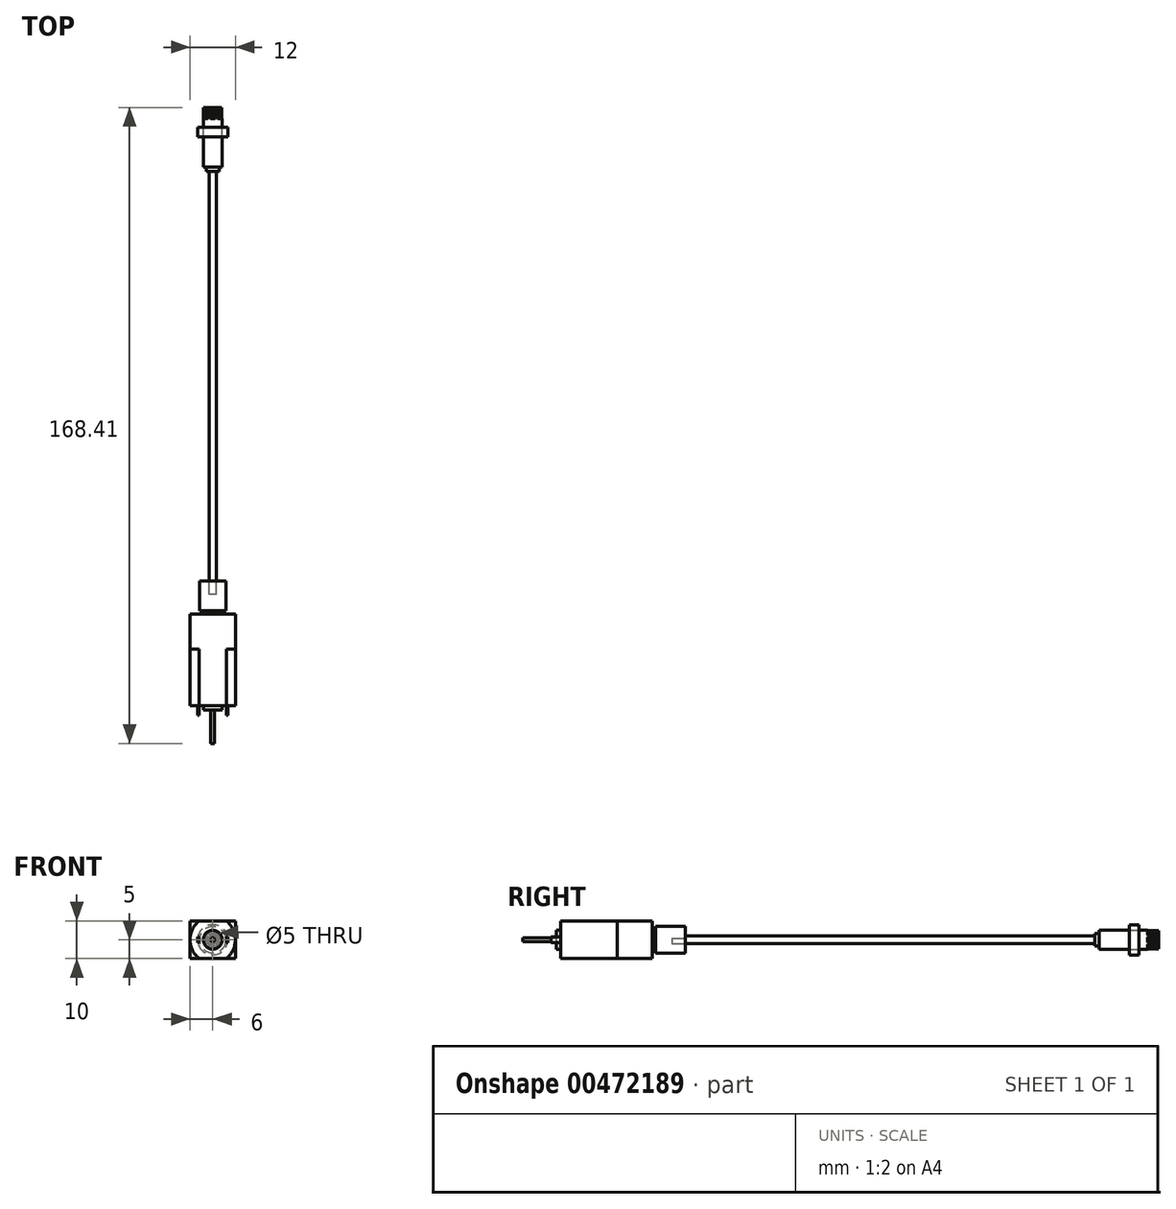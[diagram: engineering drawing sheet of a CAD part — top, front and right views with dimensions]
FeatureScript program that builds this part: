
annotation { "Feature Type Name" : "Feature", "Feature Type Description" : "" }
export const myFeature = defineFeature(function(context is Context, id is Id, definition is map)
    precondition{}
    {
        {
            var Q0;
            Q0=qCreatedBy(makeId("Right.planeOp"),FACE);
            var sketch = newSketch(context, id + "F0", { "sketchPlane" : qUnion([Q0])});
            skLineSegment(sketch, "E0.bottom", {"start": v(8.48, 0) * mm, "end": v(-8.48, 0) * mm});
            skLineSegment(sketch, "E0.top", {"start": v(8.48, 2.5) * mm, "end": v(-7.38, 2.5) * mm});
            skLineSegment(sketch, "E0.left", {"start": v(8.47, 0) * mm, "end": v(8.47, 2.5) * mm});
            skLineSegment(sketch, "E0.right", {"start": v(-8.48, 0) * mm, "end": v(-8.48, 1.7) * mm});
            skLineSegment(sketch, "E1", {"start": v(-8.48, 1.7) * mm, "end": v(-7.38, 1.7) * mm});
            skLineSegment(sketch, "E2", {"start": v(-7.38, 1.7) * mm, "end": v(-7.38, 2.5) * mm});
            skSolve(sketch);
        }
        {
            var Q0;
            Q0 = qSketchRegion(id + "F0", true);
            var Q1;
            Q1=sQuery(id+"F0.wireOp",EDGE,"E0.bottom");
            revolve(context, id + "F1", {"entities" : qUnion([Q0]), "axis" : qUnion([Q1]), "revolveType" : RevolveType.FULL});
        }
        {
            var Q0;
            Q0=makeQuery(id+"F1.opRevolve","SWEPT_FACE",FACE,{"disambiguationData":[OSD([sQuery(id+"F0.wireOp",EDGE,"E0.left")])]});
            var sketch = newSketch(context, id + "F2", { "sketchPlane" : qUnion([Q0])});
            skLineSegment(sketch, "E3", {"start": v(-0.25, 1.17) * mm, "end": v(0.25, 1.17) * mm});
            skPoint(sketch, "E4", {"position": v(0, 1.17) * mm});
            skLineSegment(sketch, "E5", {"start": v(-0.25, 1.17) * mm, "end": v(-0.6, 2.43) * mm});
            skLineSegment(sketch, "E6.MirrorCS", {"start": v(0.25, 1.17) * mm, "end": v(0.6, 2.43) * mm});
            skArc(sketch, "E7.0", {"start": v(0.6, 2.43) * mm, "mid": v(0, 2.5) * mm, "end": v(-0.6, 2.43) * mm});
            skPoint(sketch, "E8", {"position": v(0, 2.5) * mm});
            skSolve(sketch);
        }
        {
            var Q0;
            Q0 = qSketchRegion(id + "F2", true);
            extrude(context, id + "F3", {"entities" : qUnion([Q0]), "oppositeDirection" : true, "depth" : 3 * mm});
        }
        {
            var Q0;
            Q0=makeQuery(id+"F3.opExtrude","SWEPT_BODY",BODY,{"disambiguationData":[OSD([sQuery(id+"F2.wireOp",EDGE,"E3"),sQuery(id+"F2.wireOp",EDGE,"E5"),sQuery(id+"F2.wireOp",EDGE,"E6.MirrorCS"),sQuery(id+"F2.wireOp",EDGE,"E7.0")])]});
            var Q1;
            Q1=makeQuery(id+"F1.opRevolve","SWEPT_EDGE",EDGE,{"disambiguationData":[OSD([sQuery(id+"F0.wireOp",EDGE,"E0.top"),sQuery(id+"F0.wireOp",EDGE,"E0.left")])]});
            circularPattern(context, id + "F4", {"operationType" : NewBodyOperationType.REMOVE, "entities" : qUnion([Q0]), "axis" : qUnion([Q1]), "angle" : 360 * degree, "instanceCount" : 8, "equalSpace" : true});
        }
        {
            var Q0;
            Q0=qCreatedBy(makeId("Right.planeOp"),FACE);
            var sketch = newSketch(context, id + "F5", { "sketchPlane" : qUnion([Q0])});
            skLineSegment(sketch, "E9", {"start": v(3.18, 2.5) * mm, "end": v(3.18, 4) * mm});
            skLineSegment(sketch, "E10", {"start": v(3.18, 4) * mm, "end": v(0.68, 4) * mm});
            skLineSegment(sketch, "E11", {"start": v(0.68, 4) * mm, "end": v(0.68, 2.5) * mm});
            skLineSegment(sketch, "E12", {"start": v(0.68, 2.5) * mm, "end": v(3.18, 2.5) * mm});
            skSolve(sketch);
        }
        {
            var Q0;
            Q0 = qSketchRegion(id + "F5", true);
            var Q1;
            Q1=sQuery(id+"F0.wireOp",EDGE,"E0.bottom");
            revolve(context, id + "F6", {"entities" : qUnion([Q0]), "axis" : qUnion([Q1]), "revolveType" : RevolveType.FULL});
        }
        {
            var Q0;
            Q0=makeQuery(id+"F1.opRevolve","SWEPT_FACE",FACE,{"disambiguationData":[OSD([sQuery(id+"F0.wireOp",EDGE,"E0.right")])]});
            var sketch = newSketch(context, id + "F7", { "sketchPlane" : qUnion([Q0])});
            skCircle(sketch, "E13", {"center": v(0, 0) * mm, "radius": 1 * mm});
            skSolve(sketch);
        }
        {
            var Q0;
            Q0 = qSketchRegion(id + "F7", true);
            extrude(context, id + "F8", {"entities" : qUnion([Q0]), "depth" : 112.4 * mm});
        }
        {
            var Q0;
            Q0=makeQuery(id+"F8.opExtrude","CAP_FACE",FACE,{"disambiguationData":[OSD([sQuery(id+"F7.wireOp",EDGE,"E13")])],"isStart":false});
            var sketch = newSketch(context, id + "F9", { "sketchPlane" : qUnion([Q0])});
            skCircle(sketch, "E14", {"center": v(0, 0) * mm, "radius": 3.5 * mm});
            skSolve(sketch);
        }
        {
            var Q0;
            Q0 = qSketchRegion(id + "F9", true);
            extrude(context, id + "F10", {"entities" : qUnion([Q0]), "depth" : 7.8 * mm, "symmetric" : true});
        }
        {
            var Q0;
            Q0=makeQuery(id+"F10.opExtrude","CAP_FACE",FACE,{"disambiguationData":[OSD([sQuery(id+"F9.wireOp",EDGE,"E14")])],"isStart":true});
            var sketch = newSketch(context, id + "F11", { "sketchPlane" : qUnion([Q0])});
            skArc(sketch, "E15.0", {"start": v(-0.94, 0.34) * mm, "mid": v(0, -1) * mm, "end": v(0.94, 0.34) * mm});
            skLineSegment(sketch, "E16", {"start": v(-0.94, 0.34) * mm, "end": v(0.94, 0.34) * mm});
            skSolve(sketch);
        }
        {
            var Q0;
            Q0 = qSketchRegion(id + "F11", true);
            extrude(context, id + "F12", {"entities" : qUnion([Q0]), "operationType" : NewBodyOperationType.REMOVE, "oppositeDirection" : true, "depth" : 3.5 * mm});
        }
        {
            var Q0;
            Q0=makeQuery(id+"F10.opExtrude","SWEPT_BODY",BODY,{"disambiguationData":[OSD([sQuery(id+"F9.wireOp",EDGE,"E14")])]});
            var Q1;
            Q1=makeQuery(id+"F15.opExtrude","SWEPT_BODY",BODY,{"disambiguationData":[OSD([sQuery(id+"F14.wireOp",EDGE,"E17"),sQuery(id+"F14.wireOp",EDGE,"E18")])]});
            var Q2;
            Q2=makeQuery(id+"F8.opExtrude","SWEPT_BODY",BODY,{"disambiguationData":[OSD([sQuery(id+"F7.wireOp",EDGE,"E13")])]});
            booleanBodies(context, id + "F13", {"operationType" : BooleanOperationType.SUBTRACTION, "tools" : qUnion([Q0, Q1]), "targets" : qUnion([Q2]), "keepTools" : true});
        }
        {
            var Q0;
            Q0=makeQuery(id+"F10.opExtrude","CAP_FACE",FACE,{"disambiguationData":[OSD([sQuery(id+"F9.wireOp",EDGE,"E14")])],"isStart":false});
            var sketch = newSketch(context, id + "F14", { "sketchPlane" : qUnion([Q0])});
            skArc(sketch, "E17", {"start": v(-1.12, 1) * mm, "mid": v(0, -1.5) * mm, "end": v(1.12, 1) * mm});
            skLineSegment(sketch, "E18", {"start": v(-1.12, 1) * mm, "end": v(1.12, 1) * mm});
            skSolve(sketch);
        }
        {
            var Q0;
            Q0 = qSketchRegion(id + "F14", true);
            extrude(context, id + "F15", {"entities" : qUnion([Q0]), "oppositeDirection" : true, "depth" : 3.6 * mm});
        }
        {
            var Q0;
            Q0=makeQuery(id+"F15.opExtrude","SWEPT_BODY",BODY,{"disambiguationData":[OSD([sQuery(id+"F14.wireOp",EDGE,"E17"),sQuery(id+"F14.wireOp",EDGE,"E18")])]});
            var Q1;
            Q1=makeQuery(id+"F10.opExtrude","SWEPT_BODY",BODY,{"disambiguationData":[OSD([sQuery(id+"F9.wireOp",EDGE,"E14")])]});
            booleanBodies(context, id + "F16", {"operationType" : BooleanOperationType.SUBTRACTION, "tools" : qUnion([Q0]), "targets" : qUnion([Q1]), "keepTools" : true});
        }
        {
            var Q0;
            Q0=makeQuery(id+"F15.opExtrude","CAP_FACE",FACE,{"disambiguationData":[OSD([sQuery(id+"F14.wireOp",EDGE,"E17"),sQuery(id+"F14.wireOp",EDGE,"E18")])],"isStart":true});
            var sketch = newSketch(context, id + "F17", { "sketchPlane" : qUnion([Q0])});
            skCircle(sketch, "E19", {"center": v(0, 0) * mm, "radius": 2 * mm});
            skSolve(sketch);
        }
        {
            var Q0;
            Q0 = qSketchRegion(id + "F17", true);
            extrude(context, id + "F18", {"entities" : qUnion([Q0]), "operationType" : NewBodyOperationType.ADD, "depth" : 0.9 * mm});
        }
        {
            var Q0;
            Q0=makeQuery(id+"F18.opExtrude","CAP_FACE",FACE,{"disambiguationData":[OSD([sQuery(id+"F17.wireOp",EDGE,"E19")])],"isStart":false});
            var sketch = newSketch(context, id + "F19", { "sketchPlane" : qUnion([Q0])});
            skLineSegment(sketch, "E20.bottom", {"start": v(6, 5) * mm, "end": v(-6, 5) * mm});
            skLineSegment(sketch, "E20.top", {"start": v(6, -5) * mm, "end": v(-6, -5) * mm});
            skLineSegment(sketch, "E20.left", {"start": v(6, 5) * mm, "end": v(6, -5) * mm});
            skLineSegment(sketch, "E20.right", {"start": v(-6, 5) * mm, "end": v(-6, -5) * mm});
            skPoint(sketch, "E20.middle", {"position": v(0, 0) * mm});
            skSolve(sketch);
        }
        {
            var Q0;
            Q0 = qSketchRegion(id + "F19", true);
            extrude(context, id + "F20", {"entities" : qUnion([Q0]), "operationType" : NewBodyOperationType.ADD, "depth" : 24.25 * mm});
        }
        {
            var Q0;
            Q0=makeQuery(id+"F20.opExtrude","CAP_FACE",FACE,{"disambiguationData":[OSD([sQuery(id+"F19.wireOp",EDGE,"E20.bottom"),sQuery(id+"F19.wireOp",EDGE,"E20.top"),sQuery(id+"F19.wireOp",EDGE,"E20.left"),sQuery(id+"F19.wireOp",EDGE,"E20.right")])],"isStart":false});
            var sketch = newSketch(context, id + "F21", { "sketchPlane" : qUnion([Q0])});
            skPoint(sketch, "E21", {"position": v(0, 5) * mm});
            skLineSegment(sketch, "E22", {"start": v(3.6, 5) * mm, "end": v(-3.6, 5) * mm, "construction": true});
            skLineSegment(sketch, "E23", {"start": v(-3.6, -5) * mm, "end": v(3.6, -5) * mm, "construction": true});
            skPoint(sketch, "E24", {"position": v(0, -5) * mm});
            skArc(sketch, "E25", {"start": v(-3.6, 5) * mm, "mid": v(-6, 0) * mm, "end": v(-3.6, -5) * mm});
            skArc(sketch, "E26", {"start": v(3.6, -5) * mm, "mid": v(6, 0) * mm, "end": v(3.6, 5) * mm});
            skLineSegment(sketch, "E27", {"start": v(-3.6, 5) * mm, "end": v(-6, 5) * mm});
            skLineSegment(sketch, "E28", {"start": v(-6, 5) * mm, "end": v(-6, -5) * mm});
            skLineSegment(sketch, "E29", {"start": v(-6, -5) * mm, "end": v(-3.6, -5) * mm});
            skLineSegment(sketch, "E30", {"start": v(3.6, 5) * mm, "end": v(6, 5) * mm});
            skLineSegment(sketch, "E31", {"start": v(6, 5) * mm, "end": v(6, -5) * mm});
            skLineSegment(sketch, "E32", {"start": v(6, -5) * mm, "end": v(3.6, -5) * mm});
            skSolve(sketch);
        }
        {
            var Q0;
            Q0 = qSketchRegion(id + "F21", true);
            extrude(context, id + "F22", {"entities" : qUnion([Q0]), "operationType" : NewBodyOperationType.REMOVE, "oppositeDirection" : true, "depth" : 15 * mm});
        }
        {
            var Q0;
            Q0=makeQuery(id+"F20.opExtrude","CAP_FACE",FACE,{"disambiguationData":[OSD([sQuery(id+"F19.wireOp",EDGE,"E20.bottom"),sQuery(id+"F19.wireOp",EDGE,"E20.top"),sQuery(id+"F19.wireOp",EDGE,"E20.left"),sQuery(id+"F19.wireOp",EDGE,"E20.right")])],"isStart":false});
            var sketch = newSketch(context, id + "F23", { "sketchPlane" : qUnion([Q0])});
            skCircle(sketch, "E33", {"center": v(0, 0) * mm, "radius": 2.5 * mm});
            skSolve(sketch);
        }
        {
            var Q0;
            Q0 = qSketchRegion(id + "F23", true);
            extrude(context, id + "F24", {"entities" : qUnion([Q0]), "operationType" : NewBodyOperationType.ADD, "depth" : 1.2 * mm});
        }
        {
            var Q0;
            Q0=makeQuery(id+"F20.opExtrude","CAP_FACE",FACE,{"disambiguationData":[OSD([sQuery(id+"F19.wireOp",EDGE,"E20.bottom"),sQuery(id+"F19.wireOp",EDGE,"E20.top"),sQuery(id+"F19.wireOp",EDGE,"E20.left"),sQuery(id+"F19.wireOp",EDGE,"E20.right")])],"isStart":false});
            var sketch = newSketch(context, id + "F25", { "sketchPlane" : qUnion([Q0])});
            skPoint(sketch, "E34", {"position": v(0, 0) * mm});
            skLineSegment(sketch, "E35", {"start": v(-3.82, 0) * mm, "end": v(3.83, 0) * mm, "construction": true});
            skLineSegment(sketch, "E36.bottom", {"start": v(4, 0.75) * mm, "end": v(3.65, 0.75) * mm});
            skLineSegment(sketch, "E36.top", {"start": v(4, -0.75) * mm, "end": v(3.65, -0.75) * mm});
            skLineSegment(sketch, "E36.left", {"start": v(4, 0.75) * mm, "end": v(4, -0.75) * mm});
            skLineSegment(sketch, "E36.right", {"start": v(3.65, 0.75) * mm, "end": v(3.65, -0.75) * mm});
            skPoint(sketch, "E36.middle", {"position": v(3.83, 0) * mm});
            skLineSegment(sketch, "E37.bottom", {"start": v(-3.65, 0.75) * mm, "end": v(-4, 0.75) * mm});
            skLineSegment(sketch, "E37.top", {"start": v(-3.65, -0.75) * mm, "end": v(-4, -0.75) * mm});
            skLineSegment(sketch, "E37.left", {"start": v(-3.65, 0.75) * mm, "end": v(-3.65, -0.75) * mm});
            skLineSegment(sketch, "E37.right", {"start": v(-4, 0.75) * mm, "end": v(-4, -0.75) * mm});
            skPoint(sketch, "E37.middle", {"position": v(-3.82, 0) * mm});
            skSolve(sketch);
        }
        {
            var Q0;
            Q0 = qSketchRegion(id + "F25", true);
            extrude(context, id + "F26", {"entities" : qUnion([Q0]), "operationType" : NewBodyOperationType.ADD, "depth" : 2.6 * mm});
        }
        {
            var Q0;
            Q0=makeQuery(id+"F24.opExtrude","CAP_FACE",FACE,{"disambiguationData":[OSD([sQuery(id+"F23.wireOp",EDGE,"E33")])],"isStart":false});
            var sketch = newSketch(context, id + "F27", { "sketchPlane" : qUnion([Q0])});
            skCircle(sketch, "E38", {"center": v(0, 0) * mm, "radius": 0.5 * mm});
            skSolve(sketch);
        }
        {
            var Q0;
            Q0 = qSketchRegion(id + "F27", true);
            extrude(context, id + "F28", {"entities" : qUnion([Q0]), "operationType" : NewBodyOperationType.ADD, "depth" : 8.8 * mm});
        }
    });
